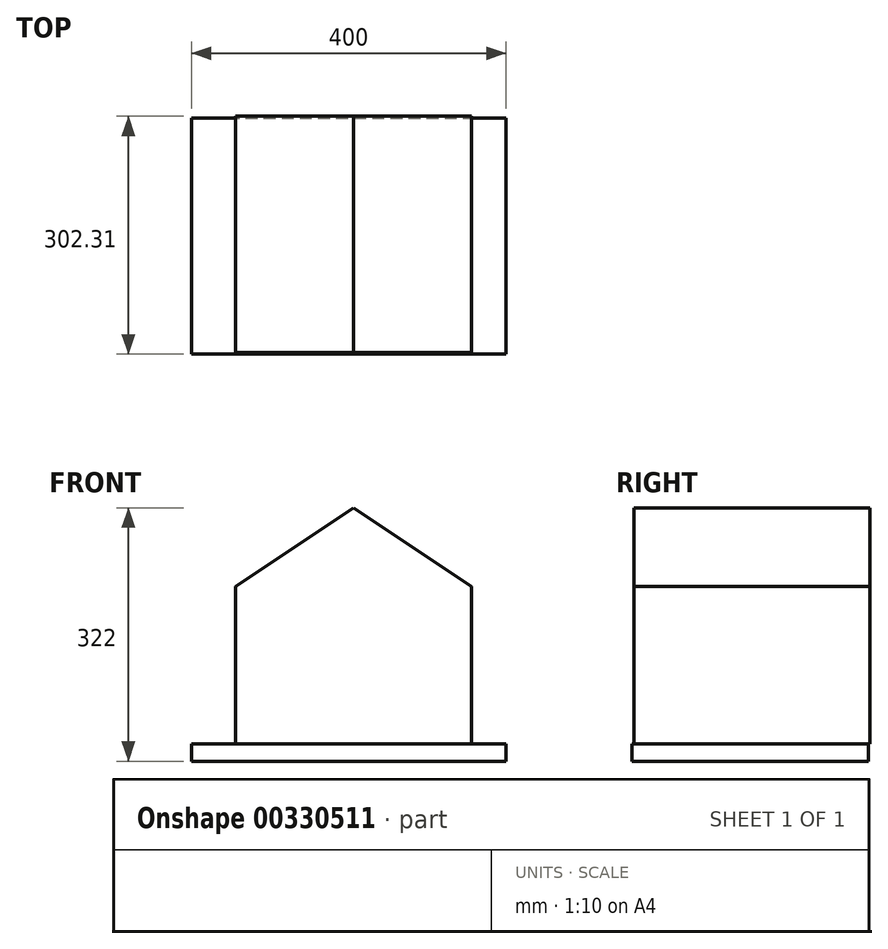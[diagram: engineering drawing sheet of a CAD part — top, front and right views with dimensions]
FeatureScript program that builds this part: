
annotation { "Feature Type Name" : "Feature", "Feature Type Description" : "" }
export const myFeature = defineFeature(function(context is Context, id is Id, definition is map)
    precondition{}
    {
        {
            var Q0;
            Q0=qCreatedBy(makeId("Front.planeOp"),FACE);
            var sketch = newSketch(context, id + "F0", { "sketchPlane" : qUnion([Q0])});
            skLineSegment(sketch, "E0.bottom", {"start": v(-150, 0) * mm, "end": v(150, 0) * mm});
            skLineSegment(sketch, "E0.top", {"start": v(-150, 200) * mm, "end": v(150, 200) * mm});
            skLineSegment(sketch, "E0.left", {"start": v(-150, 0) * mm, "end": v(-150, 200) * mm});
            skLineSegment(sketch, "E0.right", {"start": v(150, 0) * mm, "end": v(150, 200) * mm});
            skLineSegment(sketch, "E1", {"start": v(0, 200) * mm, "end": v(0, 300) * mm});
            skLineSegment(sketch, "E2", {"start": v(-150, 200) * mm, "end": v(0, 300) * mm});
            skLineSegment(sketch, "E3", {"start": v(0, 300) * mm, "end": v(150, 200) * mm});
            skSolve(sketch);
        }
        {
            var Q0;
            Q0=makeQuery(id+"F0.imprint","IMPRINT",FACE,{"disambiguationData":[TD([[makeQuery(id+"F0.imprint","IMPRINT",EDGE,{"derivedFrom":sQuery(id+"F0.wireOp",EDGE,"E0.bottom")}),1.0]])]});
            extrude(context, id + "F1", {"entities" : qUnion([Q0]), "depth" : 300 * mm});
        }
        {
            var Q0;
            Q0 = qSketchRegion(id + "F0", true);
            extrude(context, id + "F2", {"entities" : qUnion([Q0]), "operationType" : NewBodyOperationType.ADD, "depth" : 300 * mm});
        }
        {
            var Q0;
            Q0=qCreatedBy(makeId("Top.planeOp"),FACE);
            var sketch = newSketch(context, id + "F3", { "sketchPlane" : qUnion([Q0])});
            skLineSegment(sketch, "E4.bottom", {"start": v(-205.95, -2.31) * mm, "end": v(194.05, -2.31) * mm});
            skLineSegment(sketch, "E4.top", {"start": v(-205.95, -302.31) * mm, "end": v(194.05, -302.31) * mm});
            skLineSegment(sketch, "E4.left", {"start": v(-205.95, -2.31) * mm, "end": v(-205.95, -302.31) * mm});
            skLineSegment(sketch, "E4.right", {"start": v(194.05, -2.31) * mm, "end": v(194.05, -302.31) * mm});
            skSolve(sketch);
        }
        {
            var Q0;
            Q0=makeQuery(id+"F3.imprint","IMPRINT",FACE,{"disambiguationData":[TD([[makeQuery(id+"F3.imprint","IMPRINT",EDGE,{"derivedFrom":sQuery(id+"F3.wireOp",EDGE,"E4.bottom")}),-1.0]])]});
            extrude(context, id + "F4", {"entities" : qUnion([Q0]), "operationType" : NewBodyOperationType.ADD, "oppositeDirection" : true, "depth" : 22 * mm});
        }
    });
